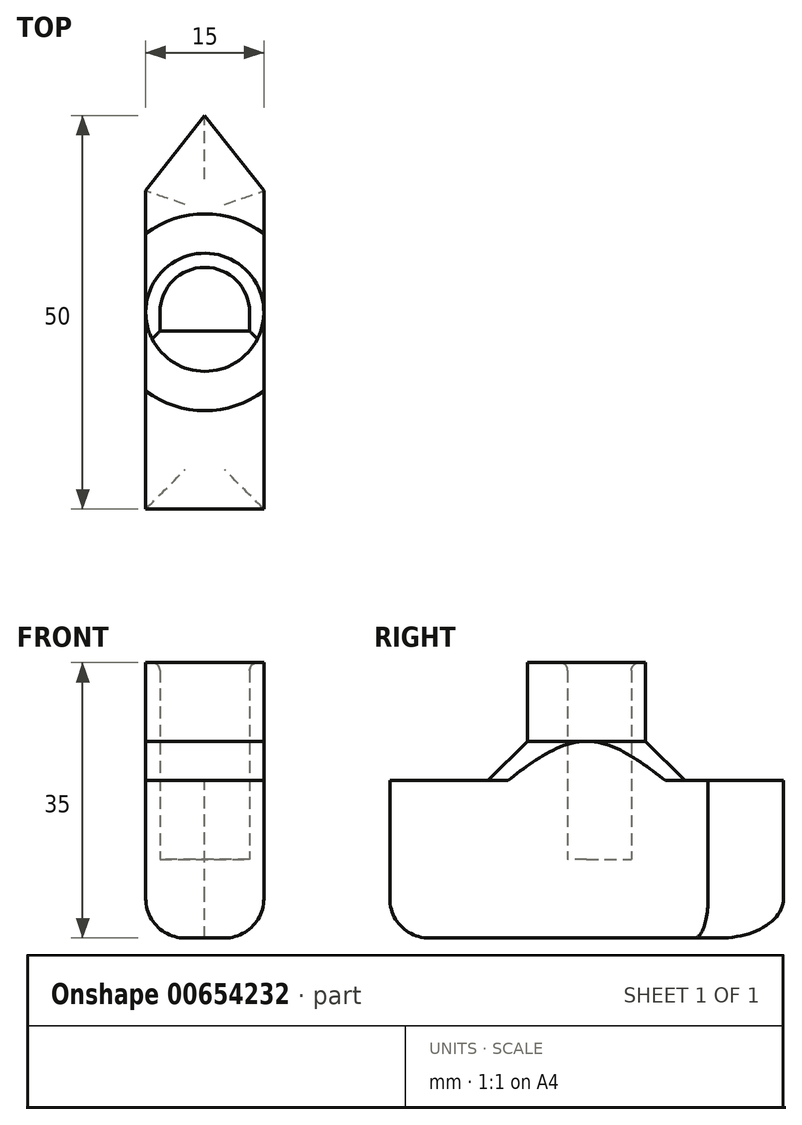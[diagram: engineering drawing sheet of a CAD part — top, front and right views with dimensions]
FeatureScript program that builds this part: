
annotation { "Feature Type Name" : "Feature", "Feature Type Description" : "" }
export const myFeature = defineFeature(function(context is Context, id is Id, definition is map)
    precondition{}
    {
        {
            var Q0;
            Q0=qCreatedBy(makeId("Top.planeOp"),FACE);
            var sketch = newSketch(context, id + "F0", { "sketchPlane" : qUnion([Q0])});
            skCircle(sketch, "E0", {"center": v(0, 0) * mm, "radius": 7.5 * mm});
            skLineSegment(sketch, "E1.top", {"start": v(-4.76, -2.4) * mm, "end": v(4.76, -2.4) * mm});
            skLineSegment(sketch, "E2.top", {"start": v(-5.7, -2.4) * mm, "end": v(-4.79, -2.4) * mm});
            skLineSegment(sketch, "E2.left", {"start": v(-5.7, 0) * mm, "end": v(-5.7, -2.4) * mm});
            skLineSegment(sketch, "E3.top", {"start": v(5.7, -2.4) * mm, "end": v(4.77, -2.4) * mm});
            skLineSegment(sketch, "E3.left", {"start": v(5.7, 0) * mm, "end": v(5.7, -2.4) * mm});
            skLineSegment(sketch, "E4.bottom", {"start": v(-5.7, -2.4) * mm, "end": v(5.7, -2.4) * mm});
            skPoint(sketch, "E4.middle", {"position": v(0, -4.82) * mm});
            skArc(sketch, "E5", {"start": v(5.7, 0) * mm, "mid": v(0, 5.7) * mm, "end": v(-5.7, 0) * mm});
            skSolve(sketch);
        }
        {
            var Q0;
            Q0=makeQuery(id+"F0.imprint","IMPRINT",FACE,{"disambiguationData":[TD([[makeQuery(id+"F0.imprint","IMPRINT",EDGE,{"derivedFrom":sQuery(id+"F0.wireOp",EDGE,"E0")}),1.0]])]});
            extrude(context, id + "F1", {"entities" : qUnion([Q0]), "depth" : 35 * mm, "offsetDistance" : 25 * mm});
        }
        {
            var Q0;
            Q0=qCreatedBy(makeId("Top.planeOp"),FACE);
            var sketch = newSketch(context, id + "F2", { "sketchPlane" : qUnion([Q0])});
            skLineSegment(sketch, "E6.bottom", {"start": v(7.5, 25) * mm, "end": v(-7.5, 25) * mm});
            skLineSegment(sketch, "E6.top", {"start": v(7.5, -25) * mm, "end": v(-7.5, -25) * mm});
            skLineSegment(sketch, "E6.left", {"start": v(7.5, 25) * mm, "end": v(7.5, -25) * mm});
            skLineSegment(sketch, "E6.right", {"start": v(-7.5, 25) * mm, "end": v(-7.5, -25) * mm});
            skPoint(sketch, "E6.middle", {"position": v(0, 0) * mm});
            skSolve(sketch);
        }
        {
            var Q0;
            Q0=makeQuery(id+"F2.imprint","IMPRINT",FACE,{"disambiguationData":[TD([[makeQuery(id+"F2.imprint","IMPRINT",EDGE,{"derivedFrom":sQuery(id+"F2.wireOp",EDGE,"E6.bottom")}),1.0]])]});
            extrude(context, id + "F3", {"entities" : qUnion([Q0]), "operationType" : NewBodyOperationType.ADD, "depth" : 20 * mm, "offsetDistance" : 25 * mm});
        }
        {
            var Q0;
            {var subQ0=sQuery(id+"F2.wireOp",EDGE,"E6.left");var subQ1=sQuery(id+"F2.wireOp",EDGE,"E6.top");var subQ2=sQuery(id+"F2.wireOp",EDGE,"E6.bottom");var subQ3=sQuery(id+"F2.wireOp",EDGE,"E6.right");Q0=makeQuery(id+"F3.boolean.opBoolean","SPLIT",FACE,{"disambiguationData":[TD([makeQuery(id+"F1.opExtrude","SWEPT_FACE",FACE,{"disambiguationData":[OSD([sQuery(id+"F0.wireOp",EDGE,"E0")])]})])],"derivedFrom":makeQuery(id+"F3.opExtrude","CAP_FACE",FACE,{"disambiguationData":[OSD([subQ2,subQ1,subQ0,subQ3])],"isStart":false})});}
            var sketch = newSketch(context, id + "F4", { "sketchPlane" : qUnion([Q0])});
            skLineSegment(sketch, "E7.bottom", {"start": v(27.9, 15.43) * mm, "end": v(-27.9, 15.43) * mm});
            skLineSegment(sketch, "E7.top", {"start": v(27.9, -15.43) * mm, "end": v(-27.9, -15.43) * mm});
            skLineSegment(sketch, "E7.left", {"start": v(27.9, 15.43) * mm, "end": v(27.9, -15.43) * mm});
            skLineSegment(sketch, "E7.right", {"start": v(-27.9, 15.43) * mm, "end": v(-27.9, -15.43) * mm});
            skPoint(sketch, "E7.middle", {"position": v(0, 0) * mm});
            skLineSegment(sketch, "E8", {"start": v(-7.5, 15.43) * mm, "end": v(0, 25) * mm});
            skLineSegment(sketch, "E9", {"start": v(0, 25) * mm, "end": v(7.5, 15.43) * mm});
            skLineSegment(sketch, "E10", {"start": v(7.5, 15.43) * mm, "end": v(-7.5, 15.43) * mm});
            skSolve(sketch);
        }
        {
            var Q0;
            {var subQ0=sQuery(id+"F4.wireOp",EDGE,"E8");Q0=makeQuery(id+"F4.imprint","IMPRINT",FACE,{"disambiguationData":[TD([[makeQuery(id+"F4.imprint","IMPRINT",EDGE,{"derivedFrom":subQ0}),1.0]])]});}
            var Q1;
            {var subQ0=sQuery(id+"F4.wireOp",EDGE,"E9");Q1=makeQuery(id+"F4.imprint","IMPRINT",FACE,{"disambiguationData":[TD([[makeQuery(id+"F4.imprint","IMPRINT",EDGE,{"derivedFrom":subQ0}),1.0]])]});}
            extrude(context, id + "F5", {"entities" : qUnion([Q0, Q1]), "operationType" : NewBodyOperationType.REMOVE, "endBound" : BoundingType.THROUGH_ALL, "oppositeDirection" : true, "depth" : 25 * mm, "offsetDistance" : 25 * mm});
        }
        {
            var Q0;
            Q0=makeQuery(id+"F5.boolean.opBoolean","INTERSECT",EDGE,{"derivedFrom":[makeQuery(id+"F3.boolean.opBoolean","MERGE",FACE,{"derivedFrom":[makeQuery(id+"F1.opExtrude","CAP_FACE",FACE,{"disambiguationData":[OSD([sQuery(id+"F0.wireOp",EDGE,"E0"),sQuery(id+"F0.wireOp",EDGE,"E2.left"),sQuery(id+"F0.wireOp",EDGE,"E3.left"),sQuery(id+"F0.wireOp",EDGE,"E4.bottom"),sQuery(id+"F0.wireOp",EDGE,"E5")])],"isStart":true}),makeQuery(id+"F3.opExtrude","CAP_FACE",FACE,{"disambiguationData":[OSD([sQuery(id+"F2.wireOp",EDGE,"E6.bottom"),sQuery(id+"F2.wireOp",EDGE,"E6.top"),sQuery(id+"F2.wireOp",EDGE,"E6.left"),sQuery(id+"F2.wireOp",EDGE,"E6.right")])],"isStart":true})]}),makeQuery(id+"F5.opExtrude","SWEPT_FACE",FACE,{"disambiguationData":[OSD([sQuery(id+"F4.wireOp",EDGE,"E9")])]})]});
            var Q1;
            Q1=makeQuery(id+"F5.boolean.opBoolean","INTERSECT",EDGE,{"derivedFrom":[makeQuery(id+"F3.boolean.opBoolean","MERGE",FACE,{"derivedFrom":[makeQuery(id+"F1.opExtrude","CAP_FACE",FACE,{"disambiguationData":[OSD([sQuery(id+"F0.wireOp",EDGE,"E0"),sQuery(id+"F0.wireOp",EDGE,"E2.left"),sQuery(id+"F0.wireOp",EDGE,"E3.left"),sQuery(id+"F0.wireOp",EDGE,"E4.bottom"),sQuery(id+"F0.wireOp",EDGE,"E5")])],"isStart":true}),makeQuery(id+"F3.opExtrude","CAP_FACE",FACE,{"disambiguationData":[OSD([sQuery(id+"F2.wireOp",EDGE,"E6.bottom"),sQuery(id+"F2.wireOp",EDGE,"E6.top"),sQuery(id+"F2.wireOp",EDGE,"E6.left"),sQuery(id+"F2.wireOp",EDGE,"E6.right")])],"isStart":true})]}),makeQuery(id+"F5.opExtrude","SWEPT_FACE",FACE,{"disambiguationData":[OSD([sQuery(id+"F4.wireOp",EDGE,"E8")])]})]});
            var Q2;
            Q2=makeQuery(id+"F3.opExtrude","CAP_EDGE",EDGE,{"disambiguationData":[OSD([sQuery(id+"F2.wireOp",EDGE,"E6.right")])],"isStart":true});
            var Q3;
            Q3=makeQuery(id+"F3.opExtrude","CAP_EDGE",EDGE,{"disambiguationData":[OSD([sQuery(id+"F2.wireOp",EDGE,"E6.left")])],"isStart":true});
            var Q4;
            Q4=makeQuery(id+"F3.opExtrude","CAP_EDGE",EDGE,{"disambiguationData":[OSD([sQuery(id+"F2.wireOp",EDGE,"E6.top")])],"isStart":true});
            var Q5;
            {var subQ0=sQuery(id+"F4.wireOp",EDGE,"E9");var subQ1=sQuery(id+"F4.wireOp",EDGE,"E8");var subQ2=sQuery(id+"F2.wireOp",EDGE,"E6.bottom");Q5=makeQuery(id+"F5.boolean.opBoolean","TWEAK_EDGE",EDGE,{"derivedFrom":[makeQuery(id+"F5.opExtrude","SWEPT_EDGE",EDGE,{"disambiguationData":[OSD([subQ2,subQ1,subQ0]),OD(0.0)]}),makeQuery(id+"F5.opExtrude","SWEPT_EDGE",EDGE,{"disambiguationData":[OSD([subQ2,subQ1,subQ0]),OD(1.0)]})]});}
            fillet(context, id + "F6", {"entities" : qUnion([Q0, Q1, Q2, Q3, Q4, Q5]), "radius" : 5 * mm, "tangentPropagation" : true, "allowEdgeOverflow" : false});
        }
        {
            var Q0;
            Q0=makeQuery(id+"F3.boolean.opBoolean","INTERSECT",EDGE,{"derivedFrom":[makeQuery(id+"F1.opExtrude","SWEPT_FACE",FACE,{"disambiguationData":[OSD([sQuery(id+"F0.wireOp",EDGE,"E0")])]}),makeQuery(id+"F3.opExtrude","CAP_FACE",FACE,{"disambiguationData":[OSD([sQuery(id+"F2.wireOp",EDGE,"E6.bottom"),sQuery(id+"F2.wireOp",EDGE,"E6.top"),sQuery(id+"F2.wireOp",EDGE,"E6.left"),sQuery(id+"F2.wireOp",EDGE,"E6.right")])],"isStart":false})]});
            chamfer(context, id + "F7", {"entities" : qUnion([Q0]), "width" : 5 * mm, "tangentPropagation" : true});
        }
        {
            var Q0;
            Q0=makeQuery(id+"F1.opExtrude","CAP_EDGE",EDGE,{"disambiguationData":[OSD([sQuery(id+"F0.wireOp",EDGE,"E5")])],"isStart":false});
            var Q1;
            Q1=makeQuery(id+"F1.opExtrude","CAP_EDGE",EDGE,{"disambiguationData":[OSD([sQuery(id+"F0.wireOp",EDGE,"E4.bottom")])],"isStart":false});
            var Q2;
            Q2=makeQuery(id+"F1.opExtrude","CAP_EDGE",EDGE,{"disambiguationData":[OSD([sQuery(id+"F0.wireOp",EDGE,"E3.left")])],"isStart":false});
            var Q3;
            Q3=makeQuery(id+"F1.opExtrude","CAP_EDGE",EDGE,{"disambiguationData":[OSD([sQuery(id+"F0.wireOp",EDGE,"E2.left")])],"isStart":false});
            fillet(context, id + "F8", {"entities" : qUnion([Q0, Q1, Q2, Q3]), "radius" : 1 * mm, "tangentPropagation" : true, "allowEdgeOverflow" : false});
        }
        {
            var Q0;
            Q0=makeQuery(id+"F3.boolean.opBoolean","SPLIT",FACE,{"disambiguationData":[TD([makeQuery(id+"F1.opExtrude","SWEPT_FACE",FACE,{"disambiguationData":[OSD([sQuery(id+"F0.wireOp",EDGE,"E2.left")])]})])],"derivedFrom":makeQuery(id+"F3.opExtrude","CAP_FACE",FACE,{"disambiguationData":[OSD([sQuery(id+"F2.wireOp",EDGE,"E6.bottom"),sQuery(id+"F2.wireOp",EDGE,"E6.top"),sQuery(id+"F2.wireOp",EDGE,"E6.left"),sQuery(id+"F2.wireOp",EDGE,"E6.right")])],"isStart":false})});
            extrude(context, id + "F9", {"entities" : qUnion([Q0]), "operationType" : NewBodyOperationType.REMOVE, "oppositeDirection" : true, "depth" : 10 * mm, "offsetDistance" : 25 * mm});
        }
    });
